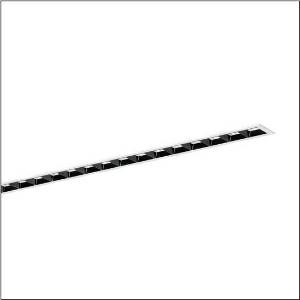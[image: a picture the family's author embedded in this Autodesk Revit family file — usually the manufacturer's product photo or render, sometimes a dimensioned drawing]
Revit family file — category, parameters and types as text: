
# Revit family: silica_r__21_51mx12tctaw_2b1a
name_source: partatom
category: Lighting Fixtures
units: mm (PartAtom-declared; Revit-internal decimal feet)

## family parameters
Cut with Voids When Loaded = No
Host = Face
Light Source = No
Part Type = Normal
Room Calculation Point = No
Round Connector Dimension = Use Diameter
Shared = No

## types (1)
- --- (1 x LED, 9300 lm, 80.4 W, 6500K)
    Apparent Load = 80 VA
    CIE Flux Codes = 84 100 100 100 100
    Color Rendering = 80
    Color Temperature = 6500K
    Default Elevation = 1800 mm
    Description = Silica® 21, office luminaire, primary light control with darklight reflector, of PMMA, black, CAT 2 (L<= 3000cd/m²), light emission: direct distribution, primary light characteristic: symmetric, installation type: recessed, LED, rated luminous flux: 9.300lm, luminous efficacy: 110lm/W, light colour: 8tw, colour temperature: 2700..6500K, control gear: DALI DT8, with terminal, 3+2-pole, max. 2.5mm², mains connection: 220..240V, AC, 50/60Hz, rated input power: 84.5W, luminaire housing, of aluminium, traffic white (RAL 9016), length: 3.028mm, width: 79mm, height: 53mm, protection rating (complete): IP20, insulation class (complete): insulation class I (protective earthing), certification: CE, ENEC, VDE, permissible operating ambient temperature: 0..+35°C, standard: EN 50419, packaging unit: 1 piece
    Height = 0 mm  [stored 0 ft]
    Lamp = 1 x LED
    Lamp Light Flux = 9300 lm
    Lamp Power = 80.4 W
    Lamp count = 1
    Length = 3027 mm
    Luminous efficacy = 116 lm/W
    Manufacturer = Siteco
    ModVariant = No
    Model = 51MX12TCTAW
    Mounting Place = Ceiling
    Mounting Type = Recessed
    Number of Poles = 1
    OnlyDefault = Yes
    Power Factor = 1
    Product Name = Silica® 21
    Product group = office luminaire | ceiling recessed
    ProductGroupID = 401
    Protection Class = Protection class I
    Protection Degree = IP 20
    RLX_Detail_Level = 1
    RLX_Emergency_Light_Flux = 0 lm
    RLX_Emergency_Type = 0
    RLX_Emergency_Type_DB = No
    RlxData = <blob elided: 59293 chars, md5=a698997d>
    Socket = socket
    Standby Power = 0 W
    System Light Flux = 9300 lm
    System Power = 80 W
    Type Comments = individual setting
    Type Image = l_1335880.jpg
    URL = http://relux.com
    VarID = @adj_140166
    Voltage = 0 V
    Weight = 0.00 kg
    Width = 79 mm

note: [stored X ft] marks values corroborated as IEEE doubles in the binary element streams (Revit-internal decimal feet)

## geometry (parser evidence)
native form markers: Blend x4, Sweep x11
no freeform markers — native parametric forms only
